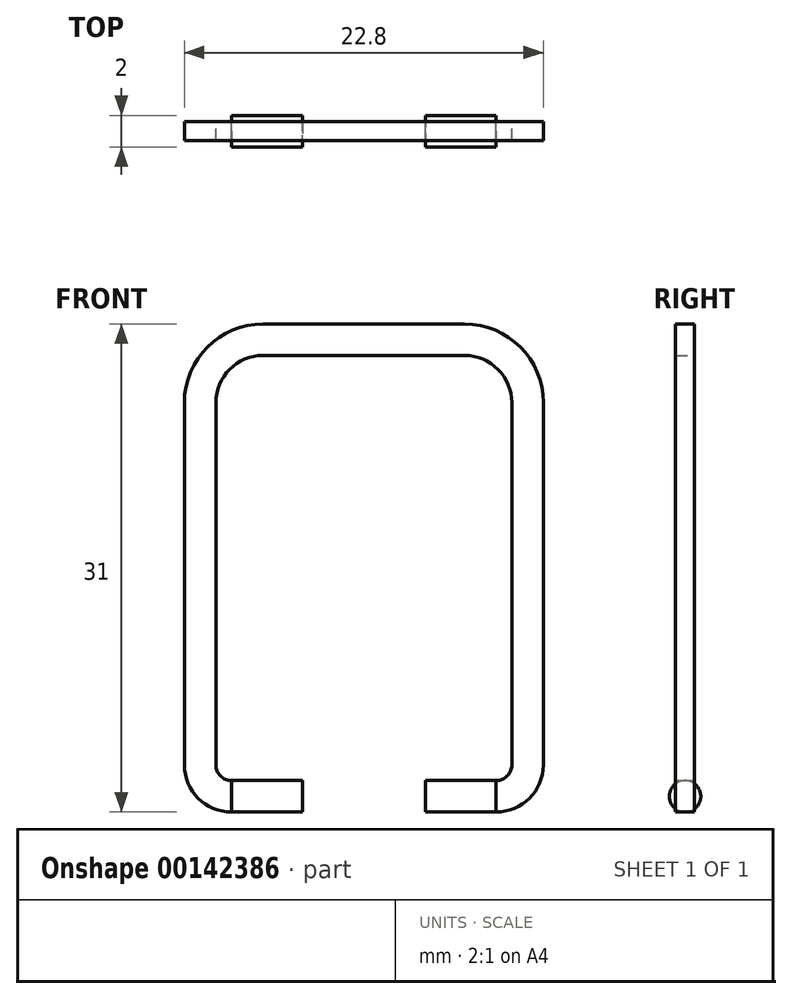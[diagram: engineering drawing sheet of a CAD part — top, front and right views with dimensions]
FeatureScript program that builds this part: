
annotation { "Feature Type Name" : "Feature", "Feature Type Description" : "" }
export const myFeature = defineFeature(function(context is Context, id is Id, definition is map)
    precondition{}
    {
        {
            var Q0;
            Q0=qCreatedBy(makeId("Front.planeOp"),FACE);
            var sketch = newSketch(context, id + "F0", { "sketchPlane" : qUnion([Q0])});
            skLineSegment(sketch, "E0", {"start": v(-7.25, 0) * mm, "end": v(5.55, 0) * mm});
            skLineSegment(sketch, "E1", {"start": v(-12.25, -5) * mm, "end": v(-12.25, -28) * mm});
            skLineSegment(sketch, "E2", {"start": v(10.55, -5) * mm, "end": v(10.55, -28) * mm});
            skLineSegment(sketch, "E3", {"start": v(-9.25, -31) * mm, "end": v(-4.75, -31) * mm});
            skLineSegment(sketch, "E4", {"start": v(7.55, -31) * mm, "end": v(3.05, -31) * mm});
            skPoint(sketch, "E5.visualSharp", {"position": v(-12.25, 0) * mm});
            skArc(sketch, "E5.filletArc", {"start": v(-7.25, 0) * mm, "mid": v(-10.79, -1.46) * mm, "end": v(-12.25, -5) * mm});
            skPoint(sketch, "E6.visualSharp", {"position": v(10.55, 0) * mm});
            skArc(sketch, "E6.filletArc", {"start": v(10.55, -5) * mm, "mid": v(9.09, -1.46) * mm, "end": v(5.55, 0) * mm});
            skLineSegment(sketch, "E7", {"start": v(0, 10.92) * mm, "end": v(0, -44.87) * mm, "construction": true});
            skPoint(sketch, "E8.visualSharp", {"position": v(-12.25, -31) * mm});
            skArc(sketch, "E8.filletArc", {"start": v(-12.25, -28) * mm, "mid": v(-11.37, -30.12) * mm, "end": v(-9.25, -31) * mm});
            skPoint(sketch, "E9.visualSharp", {"position": v(10.55, -31) * mm});
            skArc(sketch, "E9.filletArc", {"start": v(7.55, -31) * mm, "mid": v(9.67, -30.12) * mm, "end": v(10.55, -28) * mm});
            skLineSegment(sketch, "E10.0", {"start": v(7.55, -29) * mm, "end": v(3.05, -29) * mm});
            skArc(sketch, "E10.1", {"start": v(7.55, -29) * mm, "mid": v(8.26, -28.7) * mm, "end": v(8.55, -28) * mm});
            skLineSegment(sketch, "E10.2", {"start": v(8.55, -5) * mm, "end": v(8.55, -28) * mm});
            skArc(sketch, "E10.3", {"start": v(8.55, -5) * mm, "mid": v(7.67, -2.88) * mm, "end": v(5.55, -2) * mm});
            skLineSegment(sketch, "E10.4", {"start": v(-7.25, -2) * mm, "end": v(5.55, -2) * mm});
            skLineSegment(sketch, "E10.5", {"start": v(-9.25, -29) * mm, "end": v(-4.75, -29) * mm});
            skArc(sketch, "E10.6", {"start": v(-10.25, -28) * mm, "mid": v(-9.96, -28.7) * mm, "end": v(-9.25, -29) * mm});
            skLineSegment(sketch, "E10.7", {"start": v(-10.25, -5) * mm, "end": v(-10.25, -28) * mm});
            skArc(sketch, "E10.8", {"start": v(-7.25, -2) * mm, "mid": v(-9.37, -2.88) * mm, "end": v(-10.25, -5) * mm});
            skLineSegment(sketch, "E11", {"start": v(-4.75, -29) * mm, "end": v(-4.75, -31) * mm});
            skLineSegment(sketch, "E12", {"start": v(3.05, -29) * mm, "end": v(3.05, -31) * mm});
            skSolve(sketch);
        }
        {
            var Q0;
            Q0=makeQuery(id+"F0.imprint","IMPRINT",FACE,{"disambiguationData":[TD([[makeQuery(id+"F0.imprint","IMPRINT",EDGE,{"derivedFrom":sQuery(id+"F0.wireOp",EDGE,"E0")}),-1.0]])]});
            extrude(context, id + "F1", {"entities" : qUnion([Q0]), "depth" : 1.2 * mm});
        }
        {
            var Q0;
            Q0=makeQuery(id+"F1.opExtrude","SWEPT_FACE",FACE,{"disambiguationData":[OSD([sQuery(id+"F0.wireOp",EDGE,"E11")])]});
            var sketch = newSketch(context, id + "F2", { "sketchPlane" : qUnion([Q0])});
            skLineSegment(sketch, "E13.0", {"start": v(-1.2, -29) * mm, "end": v(-1.2, -31) * mm});
            skLineSegment(sketch, "E13.1", {"start": v(-1.2, -31) * mm, "end": v(0, -31) * mm});
            skLineSegment(sketch, "E13.2", {"start": v(0, -29) * mm, "end": v(0, -31) * mm});
            skLineSegment(sketch, "E13.3", {"start": v(-1.2, -29) * mm, "end": v(0, -29) * mm});
            skCircle(sketch, "E14", {"center": v(-0.6, -30) * mm, "radius": 1 * mm});
            skSolve(sketch);
        }
        {
            var Q0;
            {var subQ0=sQuery(id+"F2.wireOp",EDGE,"E14");var subQ1=sQuery(id+"F2.wireOp",EDGE,"E13.0");var subQ2=makeQuery(id+"F2.imprint","INTERSECT",VERTEX,{"disambiguationData":[OD(0.0)],"derivedFrom":[subQ1,subQ0]});Q0=makeQuery(id+"F2.imprint","IMPRINT",FACE,{"disambiguationData":[TD([[makeQuery(id+"F2.imprint","IMPRINT",EDGE,{"disambiguationData":[TD([[subQ2,-1.0]])],"derivedFrom":subQ1}),-1.0]])]});}
            var Q1;
            {var subQ0=sQuery(id+"F2.wireOp",EDGE,"E14");var subQ4=sQuery(id+"F2.wireOp",EDGE,"E13.0");var subQ5=makeQuery(id+"F2.imprint","INTERSECT",VERTEX,{"disambiguationData":[OD(0.0)],"derivedFrom":[subQ4,subQ0]});Q1=makeQuery(id+"F2.imprint","IMPRINT",FACE,{"disambiguationData":[TD([[makeQuery(id+"F2.imprint","IMPRINT",EDGE,{"disambiguationData":[TD([[subQ5,-1.0]])],"derivedFrom":subQ4}),1.0]])]});}
            var Q2;
            {var subQ0=sQuery(id+"F2.wireOp",EDGE,"E14");var subQ1=sQuery(id+"F2.wireOp",EDGE,"E13.2");var subQ2=makeQuery(id+"F2.imprint","INTERSECT",VERTEX,{"disambiguationData":[OD(0.0)],"derivedFrom":[subQ1,subQ0]});Q2=makeQuery(id+"F2.imprint","IMPRINT",FACE,{"disambiguationData":[TD([[makeQuery(id+"F2.imprint","IMPRINT",EDGE,{"disambiguationData":[TD([[subQ2,-1.0]])],"derivedFrom":subQ1}),1.0]])]});}
            extrude(context, id + "F3", {"entities" : qUnion([Q0, Q1, Q2]), "operationType" : NewBodyOperationType.ADD, "oppositeDirection" : true, "depth" : 4.5 * mm});
        }
        {
            var Q0;
            {var subQ0=sQuery(id+"F2.wireOp",EDGE,"E13.3");var subQ1=sQuery(id+"F2.wireOp",EDGE,"E13.2");var subQ2=makeQuery(id+"F2.imprint","INTERSECT",VERTEX,{"derivedFrom":[subQ1,subQ0]});Q0=makeQuery(id+"F2.imprint","IMPRINT",FACE,{"disambiguationData":[TD([[makeQuery(id+"F2.imprint","IMPRINT",EDGE,{"disambiguationData":[TD([[subQ2,-1.0]])],"derivedFrom":subQ1}),-1.0]])]});}
            var Q1;
            {var subQ0=sQuery(id+"F2.wireOp",EDGE,"E13.3");var subQ1=sQuery(id+"F2.wireOp",EDGE,"E13.0");var subQ2=makeQuery(id+"F2.imprint","INTERSECT",VERTEX,{"derivedFrom":[subQ1,subQ0]});Q1=makeQuery(id+"F2.imprint","IMPRINT",FACE,{"disambiguationData":[TD([[makeQuery(id+"F2.imprint","IMPRINT",EDGE,{"disambiguationData":[TD([[subQ2,-1.0]])],"derivedFrom":subQ1}),1.0]])]});}
            var Q2;
            {var subQ0=sQuery(id+"F2.wireOp",EDGE,"E13.2");var subQ1=sQuery(id+"F2.wireOp",EDGE,"E13.1");var subQ2=makeQuery(id+"F2.imprint","INTERSECT",VERTEX,{"derivedFrom":[subQ1,subQ0]});Q2=makeQuery(id+"F2.imprint","IMPRINT",FACE,{"disambiguationData":[TD([[makeQuery(id+"F2.imprint","IMPRINT",EDGE,{"disambiguationData":[TD([[subQ2,1.0]])],"derivedFrom":subQ1}),1.0]])]});}
            var Q3;
            {var subQ0=sQuery(id+"F2.wireOp",EDGE,"E13.1");var subQ1=sQuery(id+"F2.wireOp",EDGE,"E13.0");var subQ2=makeQuery(id+"F2.imprint","INTERSECT",VERTEX,{"derivedFrom":[subQ1,subQ0]});Q3=makeQuery(id+"F2.imprint","IMPRINT",FACE,{"disambiguationData":[TD([[makeQuery(id+"F2.imprint","IMPRINT",EDGE,{"disambiguationData":[TD([[subQ2,1.0]])],"derivedFrom":subQ1}),1.0]])]});}
            extrude(context, id + "F4", {"entities" : qUnion([Q0, Q1, Q2, Q3]), "operationType" : NewBodyOperationType.REMOVE, "oppositeDirection" : true, "depth" : 4.5 * mm});
        }
        {
            var Q0;
            Q0=makeQuery(id+"F1.opExtrude","SWEPT_FACE",FACE,{"disambiguationData":[OSD([sQuery(id+"F0.wireOp",EDGE,"E12")])]});
            var sketch = newSketch(context, id + "F5", { "sketchPlane" : qUnion([Q0])});
            skLineSegment(sketch, "E15.1", {"start": v(1.2, -29) * mm, "end": v(1.2, -31) * mm});
            skCircle(sketch, "E16", {"center": v(0.6, -30) * mm, "radius": 1 * mm});
            skSolve(sketch);
        }
        {
            var Q0;
            {var subQ0=sQuery(id+"F5.wireOp",EDGE,"E16");var subQ7=sQuery(id+"F5.wireOp",EDGE,"E15.1");var subQ8=makeQuery(id+"F5.imprint","INTERSECT",VERTEX,{"disambiguationData":[OD(0.0)],"derivedFrom":[subQ7,subQ0]});Q0=makeQuery(id+"F5.imprint","IMPRINT",FACE,{"disambiguationData":[TD([[makeQuery(id+"F5.imprint","IMPRINT",EDGE,{"disambiguationData":[TD([[subQ8,-1.0]])],"derivedFrom":subQ7}),-1.0]])]});}
            var Q1;
            {var subQ0=sQuery(id+"F5.wireOp",EDGE,"E16");var subQ1=makeQuery(id+"F1.opExtrude","CAP_EDGE",EDGE,{"disambiguationData":[OSD([sQuery(id+"F0.wireOp",EDGE,"E12")])],"isStart":true});var subQ2=makeQuery(id+"F5.imprint","INTERSECT",VERTEX,{"disambiguationData":[OD(0.0)],"derivedFrom":[subQ1,subQ0]});Q1=makeQuery(id+"F5.imprint","IMPRINT",FACE,{"disambiguationData":[TD([[makeQuery(id+"F5.imprint","IMPRINT",EDGE,{"disambiguationData":[TD([[subQ2,-1.0]])],"derivedFrom":subQ0}),1.0]])]});}
            var Q2;
            {var subQ0=sQuery(id+"F5.wireOp",EDGE,"E16");var subQ1=sQuery(id+"F5.wireOp",EDGE,"E15.1");var subQ2=makeQuery(id+"F5.imprint","INTERSECT",VERTEX,{"disambiguationData":[OD(0.0)],"derivedFrom":[subQ1,subQ0]});Q2=makeQuery(id+"F5.imprint","IMPRINT",FACE,{"disambiguationData":[TD([[makeQuery(id+"F5.imprint","IMPRINT",EDGE,{"disambiguationData":[TD([[subQ2,-1.0]])],"derivedFrom":subQ1}),1.0]])]});}
            extrude(context, id + "F6", {"entities" : qUnion([Q0, Q1, Q2]), "operationType" : NewBodyOperationType.ADD, "oppositeDirection" : true, "depth" : 4.5 * mm});
        }
        {
            var Q0;
            {var subQ0=sQuery(id+"F5.wireOp",EDGE,"E16");var subQ1=sQuery(id+"F0.wireOp",EDGE,"E12");var subQ4=makeQuery(id+"F1.opExtrude","CAP_EDGE",EDGE,{"disambiguationData":[OSD([subQ1])],"isStart":true});var subQ5=makeQuery(id+"F5.imprint","INTERSECT",VERTEX,{"disambiguationData":[OD(0.0)],"derivedFrom":[subQ4,subQ0]});Q0=makeQuery(id+"F5.imprint","IMPRINT",FACE,{"disambiguationData":[TD([[makeQuery(id+"F5.imprint","IMPRINT",EDGE,{"disambiguationData":[TD([[subQ5,1.0]])],"derivedFrom":subQ0}),-1.0]])]});}
            var Q1;
            {var subQ0=sQuery(id+"F5.wireOp",EDGE,"E15.1");var subQ3=sQuery(id+"F5.wireOp",EDGE,"E16");var subQ4=makeQuery(id+"F5.imprint","INTERSECT",VERTEX,{"disambiguationData":[OD(0.0)],"derivedFrom":[subQ0,subQ3]});Q1=makeQuery(id+"F5.imprint","IMPRINT",FACE,{"disambiguationData":[TD([[makeQuery(id+"F5.imprint","IMPRINT",EDGE,{"disambiguationData":[TD([[subQ4,1.0]])],"derivedFrom":subQ0}),-1.0]])]});}
            var Q2;
            {var subQ0=sQuery(id+"F5.wireOp",EDGE,"E16");var subQ1=sQuery(id+"F0.wireOp",EDGE,"E12");var subQ2=makeQuery(id+"F1.opExtrude","CAP_EDGE",EDGE,{"disambiguationData":[OSD([subQ1])],"isStart":true});var subQ3=makeQuery(id+"F5.imprint","INTERSECT",VERTEX,{"disambiguationData":[OD(1.0)],"derivedFrom":[subQ2,subQ0]});Q2=makeQuery(id+"F5.imprint","IMPRINT",FACE,{"disambiguationData":[TD([[makeQuery(id+"F5.imprint","IMPRINT",EDGE,{"disambiguationData":[TD([[subQ3,-1.0]])],"derivedFrom":subQ0}),-1.0]])]});}
            var Q3;
            {var subQ0=sQuery(id+"F5.wireOp",EDGE,"E15.1");var subQ3=sQuery(id+"F5.wireOp",EDGE,"E16");var subQ4=makeQuery(id+"F5.imprint","INTERSECT",VERTEX,{"disambiguationData":[OD(1.0)],"derivedFrom":[subQ0,subQ3]});Q3=makeQuery(id+"F5.imprint","IMPRINT",FACE,{"disambiguationData":[TD([[makeQuery(id+"F5.imprint","IMPRINT",EDGE,{"disambiguationData":[TD([[subQ4,-1.0]])],"derivedFrom":subQ0}),-1.0]])]});}
            extrude(context, id + "F7", {"entities" : qUnion([Q0, Q1, Q2, Q3]), "operationType" : NewBodyOperationType.REMOVE, "oppositeDirection" : true, "depth" : 4.5 * mm});
        }
    });
